# Revit family: Haworth_BeHold_PedestalTop
name_source: partatom
category: Furniture Systems
revit_build: Autodesk Revit 2018 (Build: 20170223_1515(x64)
units: mm (PartAtom-declared; Revit-internal decimal feet)

## family parameters
Always vertical = Yes
Cut with Voids When Loaded = No
OmniClass Number = 23.40.70.14.64.21
OmniClass Title = Systems Furniture
Part Type = Normal
Room Calculation Point = No
Round Connector Dimension = Use Diameter
Shared = No
Work Plane-Based = No

## types (1)
- 30d 15w
    0.75" Thick = Yes
    1.18" Thick = No
    Actual Depth = 30"
    Actual Mounting Height = 21 1/4"
    Actual Width = 15"
    Assembly Code = E2020200
    Custom Size = No
    Depth = 30"
    Description = Haworth - Be_Hold - Pedestal Top - 30d 15w
    Manufacturer = Haworth
    Max. Depth = 30"
    Max. Width = 15"
    Min. Depth = 16"
    Min. Width = 12"
    Model = Haworth Be_Hold
    Revision Number = 1
    Size = Verify Final Dim. w/ Haworth
    Standard Depths = 16, 18, 24, 30 in.
    Standard Widths = 12, 15 in.
    Sustainability Info = https://www.haworth.com
    Thickness = 3/4"
    URL = www.haworth.com
    URL - Product = https://www.haworth.com
    Warranty = http://www.haworth.com
    Width = 15"

## geometry (parser evidence)
native form markers: Sweep x3
no freeform markers — native parametric forms only
